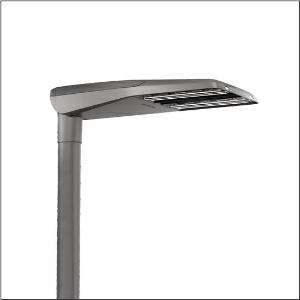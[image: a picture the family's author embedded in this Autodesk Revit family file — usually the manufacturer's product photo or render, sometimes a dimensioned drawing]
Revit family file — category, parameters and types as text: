
# Revit family: streetlight_sl_11_iq_midi___st1_2a_5xc3a61f08me_e1b3
name_source: partatom
category: Lighting Fixtures
units: mm (PartAtom-declared; Revit-internal decimal feet)

## family parameters
Cut with Voids When Loaded = No
Host = Face
Light Source = No
Part Type = Normal
Room Calculation Point = No
Round Connector Dimension = Use Diameter
Shared = No

## types (1)
- --- (1 x LED, 16120 lm, 123.9 W, 2700K)
    Apparent Load = 124 VA
    CIE Flux Codes = 32 70 96 100 100
    Color Rendering = 70
    Color Temperature = 2700K
    Default Elevation = 1800 mm
    Description = Streetlight SL 11 iQ midi, mast luminaire, primary light control with 3 zone facetted reflector, of plastic, silver coated, highly specular, primary optical cover: cover, of PMMA, transparent, light distribution: ST1.2a, light emission: direct distribution, primary light characteristic: asymmetric, installation type: post-top, side-entry, LED, High Power LED, rated luminous flux: 16.120lm, luminous efficacy: 130lm/W, light colour: 727, colour temperature: 2700K, control: Street-Remote, Auto-Match, Temp-Guard, Lumen-Switch, Night-Set, Smart-Wire, Light-Fading, Desk-Remote (wireless, voltage-free reading and setting of iQ features in the workshop via application-optimized NFC function/RFID function), optimised constant luminous flux control (CLO 2.0), with cable H07RN-F 5x 1.5mm², mains connection: 230..240V, AC, 50/60Hz, connection cable pre-assembled, cable length: 12,5m, start of lifetime: 124W, end of service life: 131W, reduction: 57W, luminaire housing, of diecast aluminium, powder-coated, Siteco® metallic grey (DB 702S), please order mast flange separately, inclination adjustable without tools: 0°, 5°, 10°, 15° (post-top) | 0°, -5°, -10°, -15° (side-entry), sealing non-destructively replaceable, multi-level sealing system, length: 780mm, width: 376mm, height: 118mm, mast flange for spigot size: 42mm (side-entry): 5XC10008XM4, 60/48mm (side-entry/post-top): 5XC10108XM2, 76/60mm (side-entry/post-top): 5XC10108XM1, equipment: Power, protection rating (complete): IP66, insulation class (complete): insulation class II (safety insulation), certification: CE, ENEC, VDE, impact resistance: IK09, permissible operating ambient temperature for outdoor applications: -25..+50°C, standard-compliant lighting for roads and squares, Environmental Product Declaration (EPD) tested and certified by an independent institute, packaging unit: 1 piece

Light Distribution: ST1.2a
    Height = 118 mm
    Lamp = 1 x LED
    Lamp Light Flux = 16120 lm
    Lamp Power = 123.9 W
    Lamp count = 1
    Length = 780 mm
    Luminous efficacy = 130 lm/W
    Manufacturer = Siteco
    ModVariant = No
    Model = 5XC3A61F08ME
    Number of Poles = 1
    OnlyDefault = Yes
    Power Factor = 1
    Product Name = Streetlight SL 11 iQ midi | ST1.2a
    Product group = mast luminaire | pylon top
    ProductGroupID = 6100
    Protection Class = Protection class II
    Protection Degree = IP 66
    RLX_Detail_Level = 1
    RLX_Emergency_Light_Flux = 0 lm
    RLX_Emergency_Type = 0
    RLX_Emergency_Type_DB = No
    RlxData = <blob elided: 70865 chars, md5=555b31ad>
    Socket = socket
    Standby Power = 0 W
    System Light Flux = 16119 lm
    System Power = 124 W
    Type Comments = factory setting: luminous flux: 100 % | dim-lin: 254 | 554 mA
    Type Image = l_1005960.jpg
    URL = http://relux.com
    VarID = @adj_010499
    Voltage = 0 V
    Weight = 0.00 kg
    Width = 376 mm

## geometry (parser evidence)
native form markers: Blend x4, Sweep x9
no freeform markers — native parametric forms only
